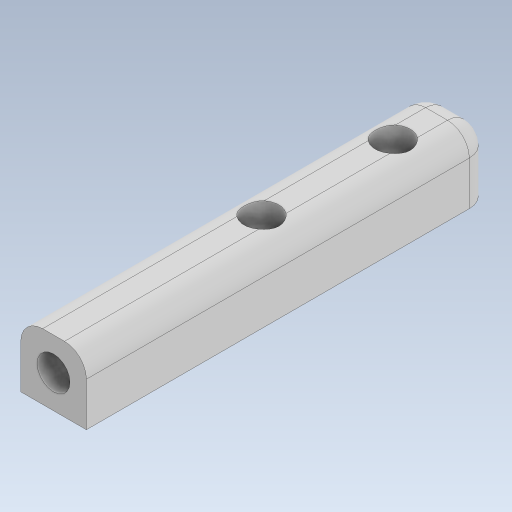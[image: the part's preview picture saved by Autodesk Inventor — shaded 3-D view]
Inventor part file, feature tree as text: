
AUTODESK INVENTOR PART (.ipt)
format: ipt  version: 2023.5 (Build 275446000, 446)  size: 313,856 bytes
history: native  units: mm
features: extrude x2, sketch x2, fillet x1
ambient origin geometry x8: Origin, YZ Plane, XZ Plane, XY Plane, X Axis, Y Axis, Z Axis, Center Point
bodies: Solid1 (feature_tree)
feature tree (5):
  extrude  "Extrusion1"  Depth=3.2mm
  extrude  "Extrusion2"  Depth=2.0mm
  fillet  "Fillet1"  Radius=6.0mm
  sketch  "Sketch1"  dims[d0=3.2mm d1=3.2mm]
  sketch  "Sketch2"  dims[d2=12.0mm d3=19.0mm d5=6.0mm d6=0.0mm d7=3.0mm d8=3.0mm d9=3.0mm d10=10.0mm d11=0.0mm d12=2.0mm]
